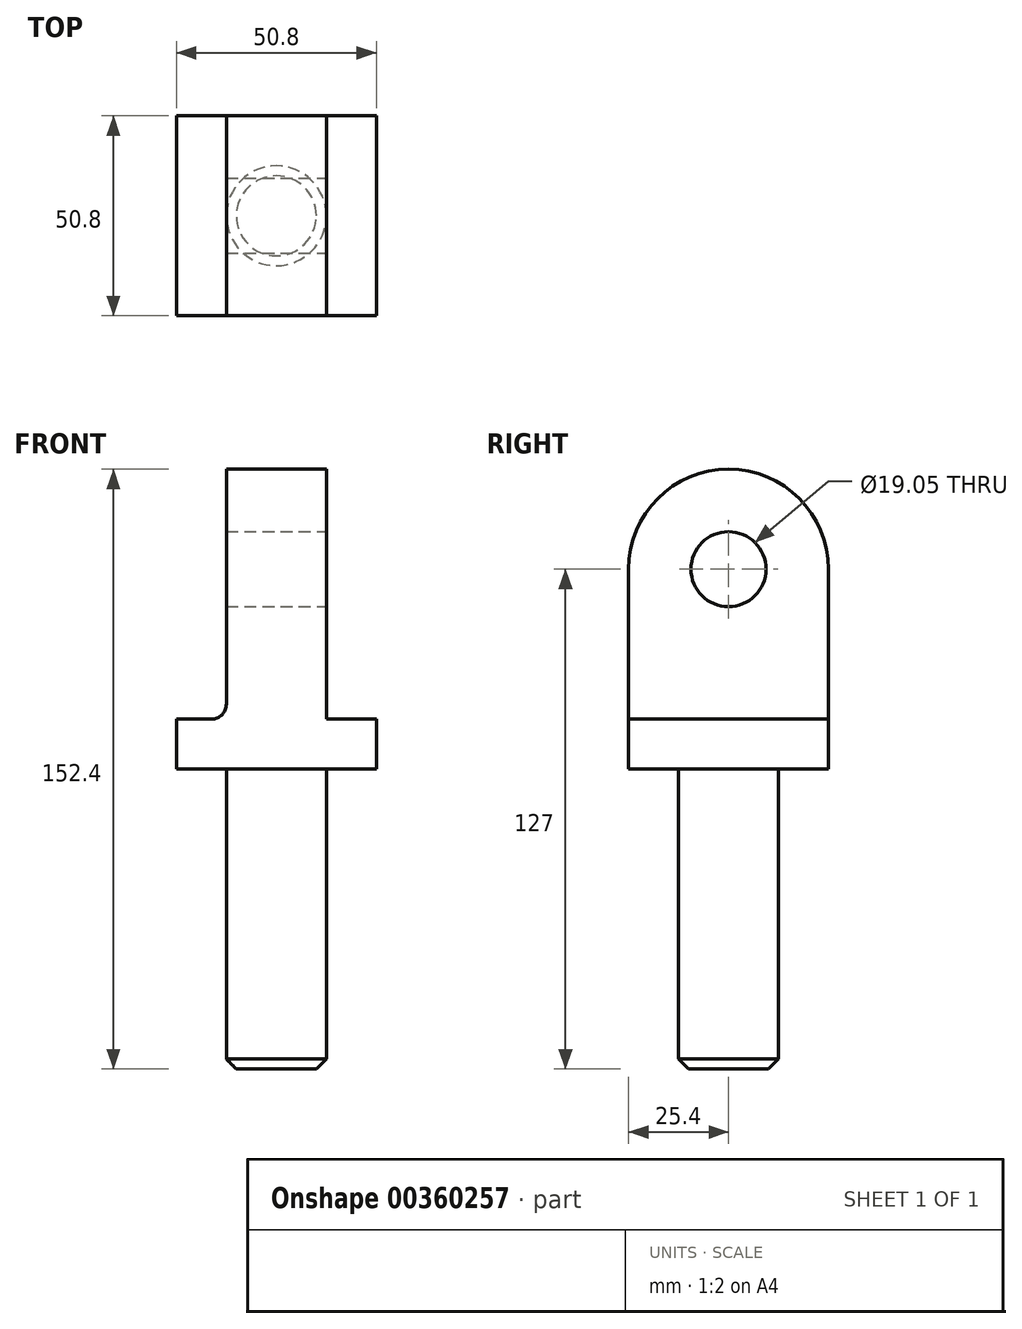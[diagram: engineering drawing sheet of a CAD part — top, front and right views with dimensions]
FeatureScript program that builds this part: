
annotation { "Feature Type Name" : "Feature", "Feature Type Description" : "" }
export const myFeature = defineFeature(function(context is Context, id is Id, definition is map)
    precondition{}
    {
        {
            var Q0;
            Q0=qCreatedBy(makeId("Top.planeOp"),FACE);
            var sketch = newSketch(context, id + "F0", { "sketchPlane" : qUnion([Q0])});
            skLineSegment(sketch, "E0.bottom", {"start": v(0, -50.8) * mm, "end": v(50.8, -50.8) * mm});
            skLineSegment(sketch, "E0.top", {"start": v(0, 0) * mm, "end": v(50.8, 0) * mm});
            skLineSegment(sketch, "E0.left", {"start": v(0, -50.8) * mm, "end": v(0, 0) * mm});
            skLineSegment(sketch, "E0.right", {"start": v(50.8, -50.8) * mm, "end": v(50.8, 0) * mm});
            skSolve(sketch);
        }
        {
            var Q0;
            Q0 = qSketchRegion(id + "F0", true);
            extrude(context, id + "F1", {"entities" : qUnion([Q0]), "depth" : 12.7 * mm});
        }
        {
            var Q0;
            Q0=makeQuery(id+"F1.opExtrude","CAP_FACE",FACE,{"disambiguationData":[OSD([sQuery(id+"F0.wireOp",EDGE,"E0.bottom"),sQuery(id+"F0.wireOp",EDGE,"E0.top"),sQuery(id+"F0.wireOp",EDGE,"E0.left"),sQuery(id+"F0.wireOp",EDGE,"E0.right")])],"isStart":true});
            var sketch = newSketch(context, id + "F2", { "sketchPlane" : qUnion([Q0])});
            skSolve(sketch);
        }
        {
            var Q0;
            Q0=makeQuery(id+"F2.imprint","IMPRINT",FACE,{"disambiguationData":[TD([[makeQuery(id+"F2.imprint","IMPRINT",EDGE,{"derivedFrom":makeQuery(id+"F1.opExtrude","CAP_EDGE",EDGE,{"disambiguationData":[OSD([sQuery(id+"F0.wireOp",EDGE,"E0.bottom")])],"isStart":true})}),-1.0]])]});
            var sketch = newSketch(context, id + "F3", { "sketchPlane" : qUnion([Q0])});
            skPoint(sketch, "E1.0", {"position": v(25.4, 50.8) * mm});
            skPoint(sketch, "E2.0", {"position": v(0, 25.4) * mm});
            skCircle(sketch, "E3", {"center": v(25.4, 25.4) * mm, "radius": 12.7 * mm});
            skSolve(sketch);
        }
        {
            var Q0;
            Q0 = qSketchRegion(id + "F3", true);
            extrude(context, id + "F4", {"entities" : qUnion([Q0]), "operationType" : NewBodyOperationType.ADD, "depth" : 76.2 * mm});
        }
        {
            var Q0;
            Q0=qCreatedBy(makeId("Right.planeOp"),FACE);
            var sketch = newSketch(context, id + "F5", { "sketchPlane" : qUnion([Q0])});
            skPoint(sketch, "E4.0", {"position": v(-25.4, 12.7) * mm});
            skLineSegment(sketch, "E5", {"start": v(-25.4, 0) * mm, "end": v(-25.4, 50.8) * mm, "construction": true});
            skLineSegment(sketch, "E6.bottom", {"start": v(-50.8, 50.8) * mm, "end": v(0, 50.8) * mm});
            skLineSegment(sketch, "E6.top", {"start": v(-50.8, 12.7) * mm, "end": v(0, 12.7) * mm});
            skLineSegment(sketch, "E6.left", {"start": v(-50.8, 50.8) * mm, "end": v(-50.8, 12.7) * mm});
            skLineSegment(sketch, "E6.right", {"start": v(0, 50.8) * mm, "end": v(0, 12.7) * mm});
            skArc(sketch, "E7", {"start": v(0, 50.8) * mm, "mid": v(-25.4, 76.2) * mm, "end": v(-50.8, 50.8) * mm});
            skSolve(sketch);
        }
        {
            var Q0;
            Q0 = qSketchRegion(id + "F5", true);
            extrude(context, id + "F6", {"entities" : qUnion([Q0]), "operationType" : NewBodyOperationType.ADD, "depth" : 38.1 * mm});
        }
        {
            var Q0;
            Q0=makeQuery(id+"F5.imprint","IMPRINT",FACE,{"disambiguationData":[TD([[makeQuery(id+"F5.imprint","IMPRINT",EDGE,{"derivedFrom":sQuery(id+"F5.wireOp",EDGE,"E6.bottom")}),1.0]])]});
            var Q1;
            Q1=makeQuery(id+"F5.imprint","IMPRINT",FACE,{"disambiguationData":[TD([[makeQuery(id+"F5.imprint","IMPRINT",EDGE,{"derivedFrom":sQuery(id+"F5.wireOp",EDGE,"E6.bottom")}),-1.0]])]});
            extrude(context, id + "F7", {"entities" : qUnion([Q0, Q1]), "operationType" : NewBodyOperationType.REMOVE, "depth" : 12.7 * mm});
        }
        {
            var Q0;
            Q0=makeQuery(id+"F6.opExtrude","CAP_FACE",FACE,{"disambiguationData":[OSD([sQuery(id+"F5.wireOp",EDGE,"E6.top"),sQuery(id+"F5.wireOp",EDGE,"E6.left"),sQuery(id+"F5.wireOp",EDGE,"E6.right"),sQuery(id+"F5.wireOp",EDGE,"E7")])],"isStart":false});
            var sketch = newSketch(context, id + "F8", { "sketchPlane" : qUnion([Q0])});
            skCircle(sketch, "E8", {"center": v(-25.4, 50.8) * mm, "radius": 9.53 * mm});
            skSolve(sketch);
        }
        {
            var Q0;
            Q0 = qSketchRegion(id + "F8", true);
            extrude(context, id + "F9", {"entities" : qUnion([Q0]), "operationType" : NewBodyOperationType.REMOVE, "endBound" : BoundingType.THROUGH_ALL, "oppositeDirection" : true, "depth" : 25.4 * mm});
        }
        {
            var Q0;
            Q0=makeQuery(id+"F6.opExtrude","CAP_EDGE",EDGE,{"disambiguationData":[OSD([sQuery(id+"F5.wireOp",EDGE,"E6.top")])],"isStart":false});
            var Q1;
            Q1=makeQuery(id+"F7.boolean.opBoolean","COPY",EDGE,{"derivedFrom":makeQuery(id+"F7.opExtrude","CAP_EDGE",EDGE,{"disambiguationData":[OSD([sQuery(id+"F5.wireOp",EDGE,"E6.top")])],"isStart":false})});
            var Q2;
            Q2=makeQuery(id+"F4.opExtrude","CAP_EDGE",EDGE,{"disambiguationData":[OSD([sQuery(id+"F3.wireOp",EDGE,"E3")])],"isStart":true});
            fillet(context, id + "F10", {"entities" : qUnion([Q0, Q1, Q2]), "radius" : 3.8 * mm, "tangentPropagation" : true, "allowEdgeOverflow" : false});
        }
        {
            var Q0;
            Q0=makeQuery(id+"F4.opExtrude","CAP_EDGE",EDGE,{"disambiguationData":[OSD([sQuery(id+"F3.wireOp",EDGE,"E3")])],"isStart":false});
            chamfer(context, id + "F11", {"entities" : qUnion([Q0]), "chamferType" : ChamferType.OFFSET_ANGLE, "width" : 2.54 * mm, "oppositeDirection" : true, "angle" : 45 * degree, "tangentPropagation" : true});
        }
    });
